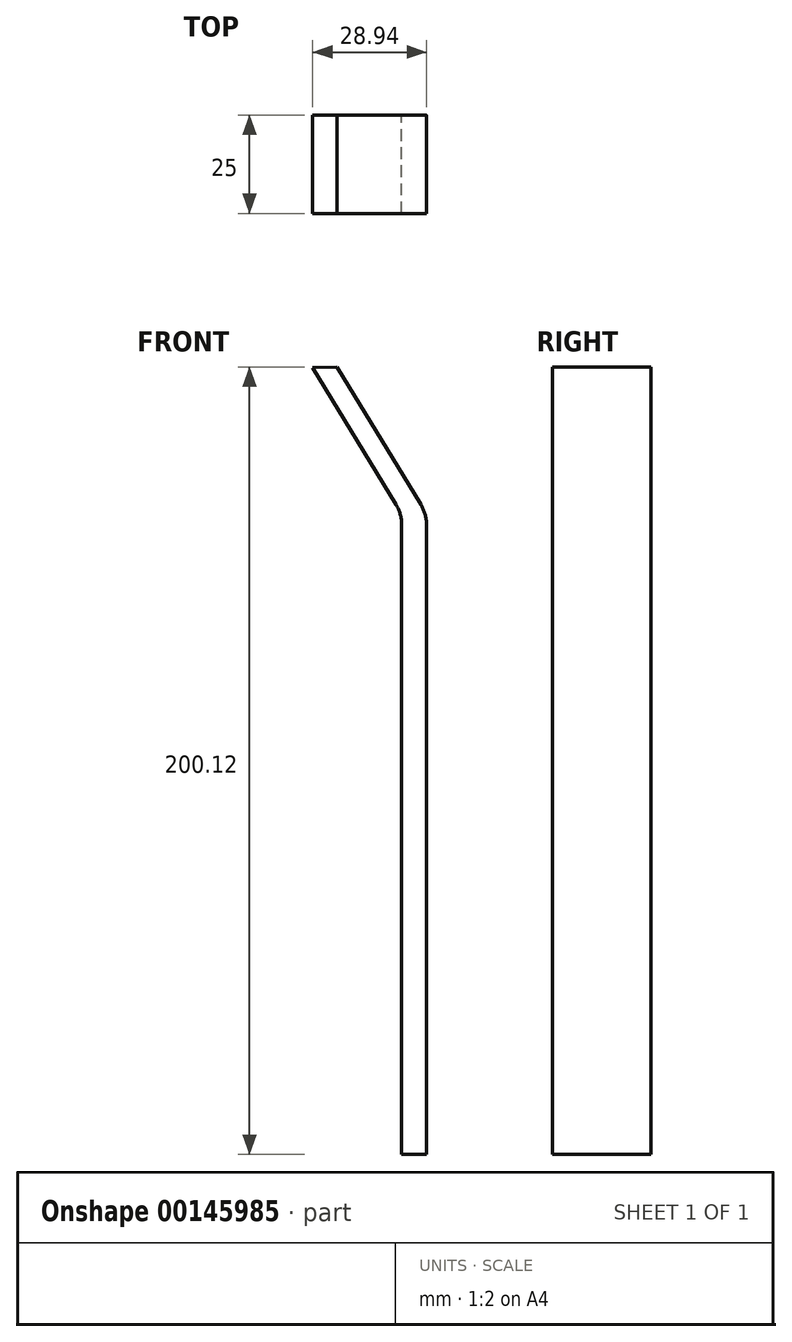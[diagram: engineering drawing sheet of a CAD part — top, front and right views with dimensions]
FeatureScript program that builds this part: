
annotation { "Feature Type Name" : "Feature", "Feature Type Description" : "" }
export const myFeature = defineFeature(function(context is Context, id is Id, definition is map)
    precondition{}
    {
        {
            var Q0;
            Q0=qCreatedBy(makeId("Front.planeOp"),FACE);
            var sketch = newSketch(context, id + "F0", { "sketchPlane" : qUnion([Q0])});
            skLineSegment(sketch, "E0", {"start": v(0, 160) * mm, "end": v(0, 0) * mm});
            skLineSegment(sketch, "E1", {"start": v(6.3, 0) * mm, "end": v(6.3, 160) * mm});
            skLineSegment(sketch, "E2", {"start": v(6.3, 162.8) * mm, "end": v(0, 162.8) * mm});
            skLineSegment(sketch, "E3", {"start": v(0, 0) * mm, "end": v(6.3, 0) * mm});
            skLineSegment(sketch, "E4", {"start": v(-22.63, 200) * mm, "end": v(-1.46, 165.2) * mm});
            skLineSegment(sketch, "E5", {"start": v(4.85, 165.2) * mm, "end": v(-16.4, 200.12) * mm});
            skLineSegment(sketch, "E6", {"start": v(-16.4, 200.12) * mm, "end": v(-22.63, 200) * mm});
            skPoint(sketch, "E7.visualSharp", {"position": v(0, 162.8) * mm});
            skArc(sketch, "E7.filletArc", {"start": v(0, 160) * mm, "mid": v(-0.37, 162.7) * mm, "end": v(-1.46, 165.2) * mm});
            skPoint(sketch, "E8.visualSharp", {"position": v(6.3, 162.8) * mm});
            skArc(sketch, "E8.filletArc", {"start": v(6.3, 160) * mm, "mid": v(5.94, 162.7) * mm, "end": v(4.85, 165.2) * mm});
            skSolve(sketch);
        }
        {
            var Q0;
            Q0=makeQuery(id+"F0.imprint","IMPRINT",FACE,{"disambiguationData":[TD([[makeQuery(id+"F0.imprint","IMPRINT",EDGE,{"derivedFrom":sQuery(id+"F0.wireOp",EDGE,"E0")}),1.0]])]});
            extrude(context, id + "F1", {"entities" : qUnion([Q0]), "depth" : 25 * mm});
        }
    });
